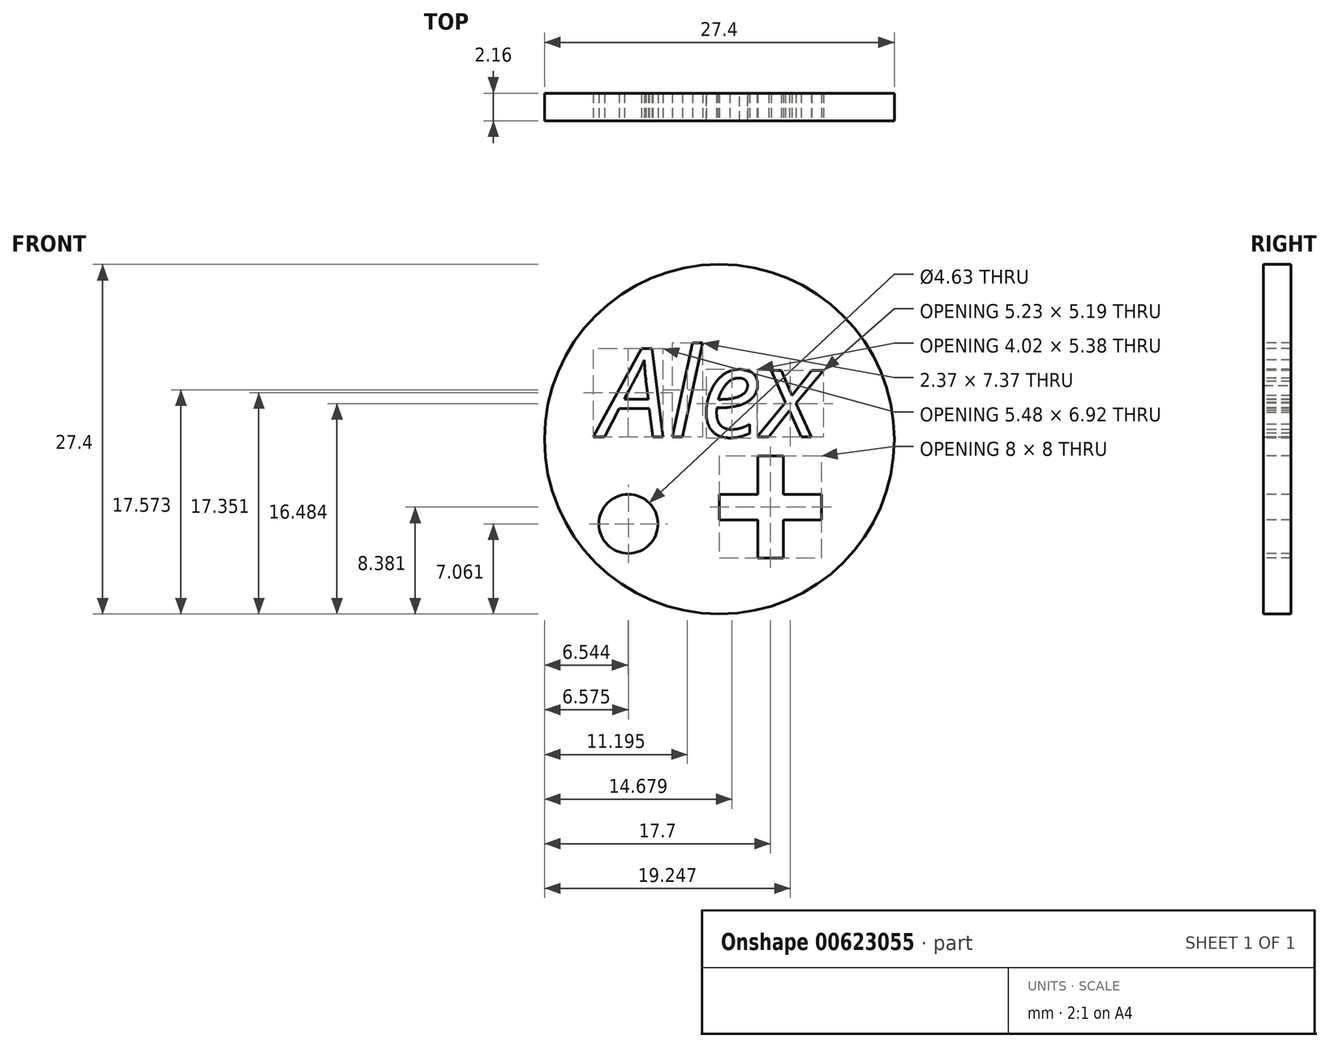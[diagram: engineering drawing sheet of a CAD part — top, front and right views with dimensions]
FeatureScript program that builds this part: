
annotation { "Feature Type Name" : "Feature", "Feature Type Description" : "" }
export const myFeature = defineFeature(function(context is Context, id is Id, definition is map)
    precondition{}
    {
        {
            var Q0;
            Q0=qCreatedBy(makeId("Front.planeOp"),FACE);
            var sketch = newSketch(context, id + "F0", { "sketchPlane" : qUnion([Q0])});
            skCircle(sketch, "E0", {"center": v(0, 0) * mm, "radius": 13.7 * mm});
            skSolve(sketch);
        }
        {
            var Q0;
            Q0 = qSketchRegion(id + "F0", true);
            extrude(context, id + "F1", {"entities" : qUnion([Q0]), "endBound" : BoundingType.SYMMETRIC, "depth" : 2.15 * mm, "offsetDistance" : 25.4 * mm});
        }
        {
            var Q0;
            Q0=makeQuery(id+"F1.opExtrude","CAP_FACE",FACE,{"disambiguationData":[OSD([sQuery(id+"F0.wireOp",EDGE,"E0")])],"isStart":false});
            var sketch = newSketch(context, id + "F2", { "sketchPlane" : qUnion([Q0])});
            skCircle(sketch, "E1", {"center": v(-7.13, -6.64) * mm, "radius": 2.31 * mm});
            skSolve(sketch);
        }
        {
            var Q0;
            Q0 = qSketchRegion(id + "F2", true);
            extrude(context, id + "F3", {"entities" : qUnion([Q0]), "operationType" : NewBodyOperationType.REMOVE, "oppositeDirection" : true, "depth" : 25 * mm, "offsetDistance" : 25 * mm});
        }
        {
            var Q0;
            Q0=makeQuery(id+"F1.opExtrude","CAP_FACE",FACE,{"disambiguationData":[OSD([sQuery(id+"F0.wireOp",EDGE,"E0")])],"isStart":false});
            var sketch = newSketch(context, id + "F4", { "sketchPlane" : qUnion([Q0])});
            skText(sketch, "E2", { "text": "Alex\n", "fontName": "OpenSans-Italic.ttf"});
            const initialGuessF4  = {"E2": [-0.00934, 0.00019, 1, 0, 0.00698]};
            skSetInitialGuess(sketch, initialGuessF4);
            skSolve(sketch);
        }
        {
            var Q0;
            Q0 = qSketchRegion(id + "F4", true);
            extrude(context, id + "F5", {"entities" : qUnion([Q0]), "operationType" : NewBodyOperationType.REMOVE, "endBound" : BoundingType.SYMMETRIC, "oppositeDirection" : true, "depth" : 25 * mm, "offsetDistance" : 25 * mm});
        }
        {
            var Q0;
            Q0=qCreatedBy(makeId("Front.planeOp"),FACE);
            var sketch = newSketch(context, id + "F6", { "sketchPlane" : qUnion([Q0])});
            skLineSegment(sketch, "E3.bottom", {"start": v(0, -4.32) * mm, "end": v(8, -4.32) * mm});
            skLineSegment(sketch, "E3.top", {"start": v(0, -6.32) * mm, "end": v(8, -6.32) * mm});
            skLineSegment(sketch, "E3.left", {"start": v(0, -4.32) * mm, "end": v(0, -6.32) * mm});
            skLineSegment(sketch, "E3.right", {"start": v(8, -4.32) * mm, "end": v(8, -6.32) * mm});
            skPoint(sketch, "E3.middle", {"position": v(4, -5.32) * mm});
            skLineSegment(sketch, "E4.bottom", {"start": v(3, -1.32) * mm, "end": v(5, -1.32) * mm});
            skLineSegment(sketch, "E4.top", {"start": v(3, -9.32) * mm, "end": v(5, -9.32) * mm});
            skLineSegment(sketch, "E4.left", {"start": v(3, -1.32) * mm, "end": v(3, -9.32) * mm});
            skLineSegment(sketch, "E4.right", {"start": v(5, -1.32) * mm, "end": v(5, -9.32) * mm});
            skSolve(sketch);
        }
        {
            var Q0;
            Q0 = qSketchRegion(id + "F6", true);
            extrude(context, id + "F7", {"entities" : qUnion([Q0]), "operationType" : NewBodyOperationType.REMOVE, "oppositeDirection" : true, "depth" : 25 * mm, "offsetDistance" : 25 * mm});
        }
        {
            var Q0;
            Q0 = qSketchRegion(id + "F6", true);
            extrude(context, id + "F8", {"entities" : qUnion([Q0]), "operationType" : NewBodyOperationType.REMOVE, "endBound" : BoundingType.UP_TO_NEXT, "depth" : 0.1 * mm, "offsetDistance" : 25 * mm});
        }
    });
